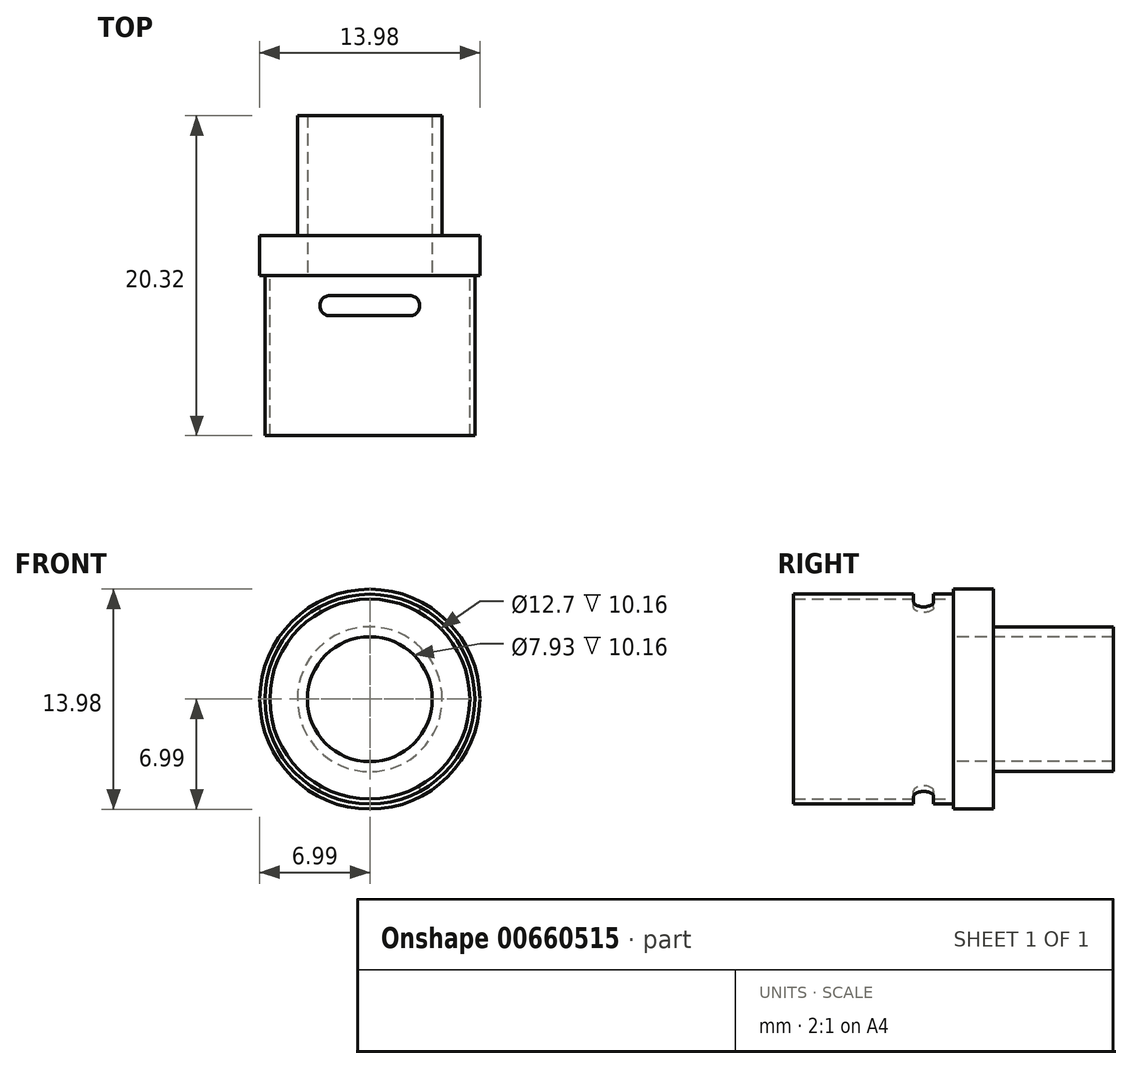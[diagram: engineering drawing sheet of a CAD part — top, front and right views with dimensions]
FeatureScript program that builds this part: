
annotation { "Feature Type Name" : "Feature", "Feature Type Description" : "" }
export const myFeature = defineFeature(function(context is Context, id is Id, definition is map)
    precondition{}
    {
        {
            var Q0;
            Q0=qCreatedBy(makeId("Front.planeOp"),FACE);
            var sketch = newSketch(context, id + "F0", { "sketchPlane" : qUnion([Q0])});
            skCircle(sketch, "E0", {"center": v(0, 0) * mm, "radius": 3.96 * mm});
            skCircle(sketch, "E1", {"center": v(0, 0) * mm, "radius": 4.6 * mm});
            skCircle(sketch, "E2", {"center": v(0, 0) * mm, "radius": 6.99 * mm});
            skCircle(sketch, "E3", {"center": v(0, 0) * mm, "radius": 6.35 * mm});
            skSolve(sketch);
        }
        {
            var Q0;
            Q0=makeQuery(id+"F0.imprint","IMPRINT",FACE,{"disambiguationData":[TD([[makeQuery(id+"F0.imprint","IMPRINT",EDGE,{"derivedFrom":sQuery(id+"F0.wireOp",EDGE,"E0")}),-1.0]])]});
            extrude(context, id + "F1", {"entities" : qUnion([Q0]), "oppositeDirection" : true, "depth" : 7.62 * mm, "offsetDistance" : 25.4 * mm});
        }
        {
            var Q0;
            Q0=makeQuery(id+"F0.imprint","IMPRINT",FACE,{"disambiguationData":[TD([[makeQuery(id+"F0.imprint","IMPRINT",EDGE,{"derivedFrom":sQuery(id+"F0.wireOp",EDGE,"E2")}),1.0]])]});
            var Q1;
            Q1=makeQuery(id+"F0.imprint","IMPRINT",FACE,{"disambiguationData":[TD([[makeQuery(id+"F0.imprint","IMPRINT",EDGE,{"derivedFrom":sQuery(id+"F0.wireOp",EDGE,"E1")}),-1.0]])]});
            var Q2;
            Q2=makeQuery(id+"F0.imprint","IMPRINT",FACE,{"disambiguationData":[TD([[makeQuery(id+"F0.imprint","IMPRINT",EDGE,{"derivedFrom":sQuery(id+"F0.wireOp",EDGE,"G8IfupT2-PCPL-Ad0W-qswr-mcryHzEn2Uvm")}),-1.0]])]});
            var Q3;
            Q3=makeQuery(id+"F0.imprint","IMPRINT",FACE,{"disambiguationData":[TD([[makeQuery(id+"F0.imprint","IMPRINT",EDGE,{"derivedFrom":sQuery(id+"F0.wireOp",EDGE,"E0")}),-1.0]])]});
            extrude(context, id + "F2", {"entities" : qUnion([Q0, Q1, Q2, Q3]), "operationType" : NewBodyOperationType.ADD, "depth" : 2.54 * mm, "offsetDistance" : 25.4 * mm});
        }
        {
            var Q0;
            Q0=makeQuery(id+"F0.imprint","IMPRINT",FACE,{"disambiguationData":[TD([[makeQuery(id+"F0.imprint","IMPRINT",EDGE,{"derivedFrom":sQuery(id+"F0.wireOp",EDGE,"E2")}),1.0]])]});
            extrude(context, id + "F3", {"entities" : qUnion([Q0]), "operationType" : NewBodyOperationType.ADD, "depth" : 12.7 * mm, "offsetDistance" : 25.4 * mm});
        }
        {
            var Q0;
            Q0=qCreatedBy(makeId("Top.planeOp"),FACE);
            var sketch = newSketch(context, id + "F4", { "sketchPlane" : qUnion([Q0])});
            skLineSegment(sketch, "E4", {"start": v(0, 0) * mm, "end": v(0, -4.22) * mm, "construction": true});
            skLineSegment(sketch, "E5", {"start": v(0, -3.81) * mm, "end": v(2.54, -3.81) * mm});
            skLineSegment(sketch, "E6", {"start": v(0, -5.08) * mm, "end": v(2.54, -5.08) * mm});
            skArc(sketch, "E7", {"start": v(2.54, -5.08) * mm, "mid": v(3.17, -4.45) * mm, "end": v(2.54, -3.81) * mm});
            skArc(sketch, "E8.MirrorCS", {"start": v(-2.54, -5.08) * mm, "mid": v(-3.18, -4.45) * mm, "end": v(-2.54, -3.81) * mm});
            skLineSegment(sketch, "E9.MirrorCS", {"start": v(0, -5.08) * mm, "end": v(-2.54, -5.08) * mm});
            skLineSegment(sketch, "E10.MirrorCS", {"start": v(0, -3.81) * mm, "end": v(-2.54, -3.81) * mm});
            skSolve(sketch);
        }
        {
            var Q0;
            Q0=makeQuery(id+"F3.opExtrude","CAP_FACE",FACE,{"disambiguationData":[OSD([sQuery(id+"F0.wireOp",EDGE,"E2"),sQuery(id+"F0.wireOp",EDGE,"E3")])],"isStart":false});
            var sketch = newSketch(context, id + "F5", { "sketchPlane" : qUnion([Q0])});
            skCircle(sketch, "E11", {"center": v(0, 0) * mm, "radius": 6.67 * mm});
            skCircle(sketch, "E12", {"center": v(0, 0) * mm, "radius": 6.99 * mm});
            skSolve(sketch);
        }
        {
            var Q0;
            Q0=makeQuery(id+"F5.imprint","IMPRINT",FACE,{"disambiguationData":[TD([[makeQuery(id+"F5.imprint","IMPRINT",EDGE,{"derivedFrom":sQuery(id+"F5.wireOp",EDGE,"E11")}),-1.0]])]});
            extrude(context, id + "F6", {"entities" : qUnion([Q0]), "operationType" : NewBodyOperationType.REMOVE, "oppositeDirection" : true, "depth" : 10.16 * mm, "offsetDistance" : 25.4 * mm});
        }
        {
            var Q0;
            Q0 = qSketchRegion(id + "F4", true);
            extrude(context, id + "F7", {"entities" : qUnion([Q0]), "operationType" : NewBodyOperationType.REMOVE, "endBound" : BoundingType.SYMMETRIC, "oppositeDirection" : true, "depth" : 13.65 * mm, "offsetDistance" : 25.4 * mm});
        }
    });
